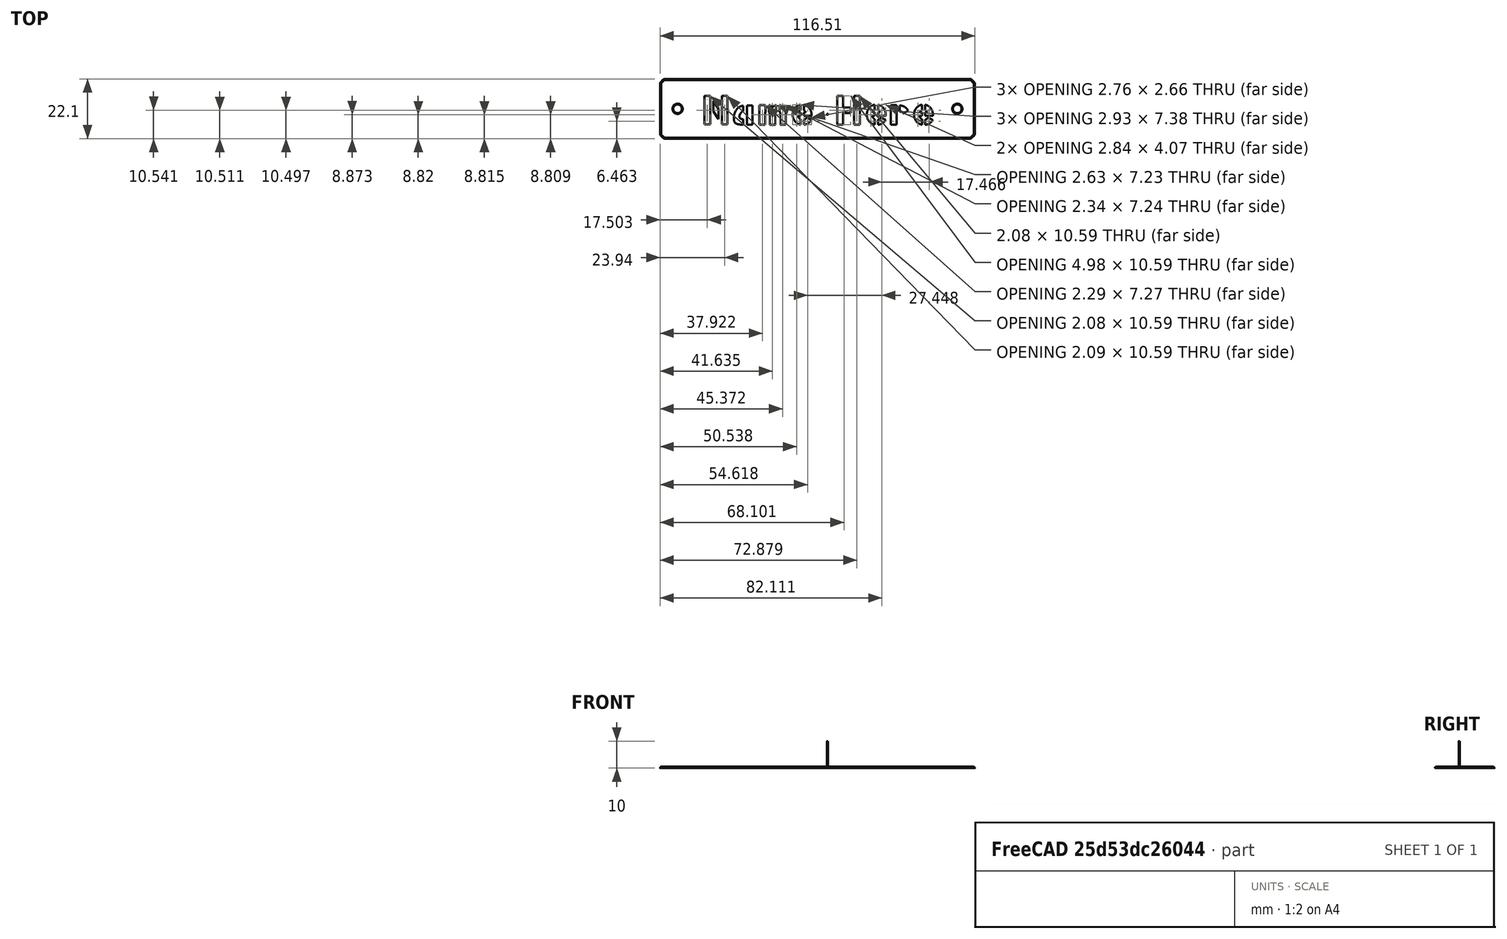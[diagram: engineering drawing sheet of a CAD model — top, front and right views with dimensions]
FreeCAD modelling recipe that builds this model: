
FCSTD DOCUMENT  (FreeCAD 0.18R4 (GitTag))
Label: patreon-3D-print-badges
License: CreativeCommons Attribution-ShareAlike
LicenseURL: http://creativecommons.org/licenses/by-sa/4.0/
objects: Part::Part2DObjectPython×2, Part::Extrusion×2, Part::Cylinder×2, Part::Cut×2, PartDesign::Chamfer×2, Spreadsheet::Sheet×1, Part::FeaturePython×1, PartDesign::FeatureBase×1, PartDesign::Fillet×1, PartDesign::Body×1
note: 14 computed .brp shape members not serialized (recipe doc carries the construction recipe); baked Part::Feature solids carry a one-line shape summary decoded from their .brp

FEATURE [Part::Part2DObjectPython] ShapeString  # Draft 2D object (typed FeaturePython)
  FontFile = <userpath>/Downloads/Cylincilo-font-master/Cylincilo-font-master/Cylincilo.ttf
  Placement = pos=(15.5,5.2,0) rot=(0,0,1;0rad)
  Size = 12.2
  String = Name Here
  Tracking = 0.7
  expr: Placement.Base.y = Spreadsheet.Margin_bottom
  expr: Placement.Base.x = Spreadsheet.Margin_left_and_rigth
  expr: Size = Spreadsheet.Font_heigth
FEATURE [Spreadsheet::Sheet] Spreadsheet
  cells = A1=Thickness; B1(Thickness)=0.6; A2=Margin top; B2(Margin_top)=4.7; A3=Margin bottom; B3(Margin_bottom)=5.2; A4=Margin left and rigth; B4(Margin_left_and_rigth)=15.5; A5=Hole size; B5(Hole_size)=3.2; A6=Hole dist; B6(Hole_dist)=6.5; A7=Font heigth; B7(Font_heigth)=12.2; A8=Chamfer; B8(Chamfer)=0.4; A9=Fillet; B9(Fillet)=2; A10=Hole straight; B10(Hole_straight)=0.3
FEATURE [Part::Part2DObjectPython] Rectangle  # Draft 2D object (typed FeaturePython)
  ChamferSize = 2
  Columns = 1
  FilletRadius = 0
  Height = 22.1
  Length = 116.511
  MakeFace = true
  Rows = 1
  expr: ChamferSize = Spreadsheet.Fillet
  expr: Height = ShapeString.Size + Spreadsheet.Margin_bottom * 1mm + Spreadsheet.Margin_top * 1mm
  expr: Length = ShapeString.Shape.BoundBox.XLength + Spreadsheet.Margin_left_and_rigth * 2 + Spreadsheet.Font_heigth * 0.08
FEATURE [Part::Extrusion] Extrude  label="Extrude box"
  Base = -> Rectangle
  Dir = (0,0,1)
  DirMode = 2
  FaceMakerClass = Part::FaceMakerBullseye
  LengthFwd = 0.6
  LengthRev = 0
  Solid = false
  Symmetric = false
  expr: LengthFwd = Spreadsheet.Thickness
FEATURE [Part::Extrusion] Extrude001  label="Extrude text"
  Base = -> ShapeString
  Dir = (0,0,1)
  DirMode = 2
  FaceMakerClass = Part::FaceMakerBullseye
  LengthFwd = 0.6
  LengthRev = 0
  Solid = false
  Symmetric = false
  expr: LengthFwd = Spreadsheet.Thickness
FEATURE [Part::Cylinder] Cylinder
  Angle = 360
  AttacherType = Attacher::AttachEngine3D
  Height = 10
  Placement = pos=(6.5,11.05,0) rot=(0,0,1;0rad)
  Radius = 1.6
  expr: Radius = Spreadsheet.Hole_size / 2
  expr: Placement.Base.y = Rectangle.Height / 2
  expr: Placement.Base.x = Spreadsheet.Hole_dist
FEATURE [Part::FeaturePython] Array  label="Array holes"  # Draft array (typed FeaturePython)
  Angle = 360
  ArrayType = 0
  Axis = (0,0,1)
  Base = -> Cylinder
  Center = (0,0,0)
  Fuse = false
  IntervalAxis = (0,0,0)
  IntervalX = (103.511,0,0)
  IntervalY = (0,1,0)
  IntervalZ = (0,0,1)
  NumberPolar = 1
  NumberX = 2
  NumberY = 1
  NumberZ = 1
  expr: IntervalX.x = Rectangle.Length - Spreadsheet.Hole_dist * 2mm
FEATURE [Part::Cut] Cut  label="Cut holes in box"
  Base = -> Extrude
  Tool = -> Array
FEATURE [PartDesign::FeatureBase] BaseFeature
  BaseFeature = -> Cut
FEATURE [Part::Cylinder] Cylinder001  label="Nozzle viz"
  Angle = 360
  AttacherType = Attacher::AttachEngine3D
  Height = 10
  Placement = pos=(62,9,0) rot=(0,0,1;0rad)
  Radius = 0.2
FEATURE [PartDesign::Fillet] Fillet
  Base = -> BaseFeature [Edge25,Edge27,Edge5,Edge1,Edge2,Edge8,Edge26,Edge28]
  BaseFeature = -> BaseFeature
  Radius = 1
  expr: Radius = Spreadsheet.Fillet / 2
FEATURE [PartDesign::Chamfer] Chamfer
  Base = -> Fillet [Edge4,Edge23,Edge25,Edge26,Edge27,Edge28,Edge29,Edge30,Edge31,Edge32,Edge33,Edge34,Edge35,Edge36,Edge37,Edge38]
  BaseFeature = -> Fillet
  Size = 0.4
  expr: Size = Spreadsheet.Chamfer
FEATURE [PartDesign::Chamfer] Chamfer001
  Base = -> Chamfer [Edge47,Edge48]
  BaseFeature = -> Chamfer
  Size = 0.3
  expr: Size = Spreadsheet.Thickness - Spreadsheet.Hole_straight
FEATURE [PartDesign::Body] Body  label="Body for chamfering"
  BaseFeature = -> Cut
  Group = -> [BaseFeature,Fillet,Chamfer,Chamfer001]
  Origin = -> Origin
  Tip = -> Chamfer001
FEATURE [Part::Cut] Cut001  label="Cut text into box"
  Base = -> Body
  Tool = -> Extrude001
